# Revit family: RN 81037 Optipress-Aquaplus-Übergang
name_source: partatom
category: Rohrformteile
units: mm (PartAtom-declared; Revit-internal decimal feet)

## family parameters
Arbeitsebenenbasiert = Nein
Beim Laden mit Abzugskörper schneiden = Nein
Bemaßung runder Anschluss = Durchmesser verwenden
Gemeinsam genutzt = Nein
Immer vertikal = Ja
Teiletyp = Verbindung

## types (9) — shared parameters
1.010.00.2 Blattnummer der Richtlinie = 29
1.010.00.3 Ausgabedatum (Monat) der Richtlinie = 201308
1.010.00.4 Herstellername = R. Nussbaum AG
1.010.00.5 Revisionsdatum der Datei = 20190521
1.010.00.6 Webadresse des Herstellers = http://www.nussbaum.ch
1.100.00.4 Produktbezeichnung = Versorgung
1.110.00.2 Index = 4
1.110.00.4 Produktbezeichnung = Optipress
1.960/3L.00.8 Link (URL) = https://www.nussbaum.ch
29.700.00.4 Produktname = Optipress-Aquaplus-Übergang, für flachdichtende Verschraubungen
29.700.00.5 Produktkennung = 2
29.700.00.6 Querschnittsform = 1
29.700.00.7 Nennweitensystem = DN
29.700.00.8 Nenndrucksystem = PN
29.710.02.4 Nenndruck = 16
29.710.02.5 max. zul. Überdruck [hPa] = 1600
29.710.02.7 max. zul. Dauer-Betriebsdruck [hPa] = 1600
29.710.02.9 max. zul. Dauer-Betriebstemperatur [°C] = 95
Connector Visibility = Nein
EnclosingSpace Visibility = Nein

## per-type parameters (varying)
| type | 1.800.00.3 TGA-Nummer | 1.810.00.3 Hersteller-Bestellnummer | 1.810.00.4 DATANORM-Nummer | 1.810.00.5 StLB-Nummer | 1.810.00.6 GTIN-Nummer | 29.710.02.10 Formstück-Gewicht [kg] | 29.710.02.3 Benennung | CONNECTOR0_DIAMETER_dX_0r | CONNECTOR0_dX_01 | CONNECTOR0_ref_dX | CONNECTOR1_DIAMETER_dX_0r | CONNECTOR1_dX_00 | CONNECTOR1_dX_01 | CONNECTOR1_ref_dX | R. Nussbaum AG 81037.21 de Visibility | R. Nussbaum AG 81037.22 de Visibility | R. Nussbaum AG 81037.23 de Visibility | R. Nussbaum AG 81037.24 de Visibility | R. Nussbaum AG 81037.25 de Visibility | R. Nussbaum AG 81037.26 de Visibility | R. Nussbaum AG 81037.27 de Visibility | R. Nussbaum AG 81037.28 de Visibility | R. Nussbaum AG 81037.29 de Visibility |
| 81037.21, Optipress-Aquaplus-Übergang, für flachdichtende Verschraubungen, DN=12x15, L=43 | 01900400000000000000000000000000000000000000000039000000000000000001 | 81037.21 | 81037.21 | 266.553 | 7612945713803 | 0.041 | Optipress-Aquaplus-Übergang, für flachdichtende Verschraubungen, DN=12x15, L=43 | 12 mm  [stored 0.0393701 ft] | 22 mm | 22 mm | 15 mm  [stored 0.0492126 ft] | 30 mm  [stored 0.0984252 ft] | 43 mm  [stored 0.141076 ft] | 30 mm  [stored 0.0984252 ft] | Ja | Nein | Nein | Nein | Nein | Nein | Nein | Nein | Nein |
| 81037.22, Optipress-Aquaplus-Übergang, für flachdichtende Verschraubungen, DN=15x20, L=49 | 01900400000000000000000000000000000000000000000039000000000000000002 | 81037.22 | 81037.22 | 266.553 | 7612945654274 | 0.059 | Optipress-Aquaplus-Übergang, für flachdichtende Verschraubungen, DN=15x20, L=49 | 15 mm  [stored 0.0492126 ft] | 22 mm | 22 mm | 20 mm | 28 mm | 43 mm  [stored 0.141076 ft] | 28 mm | Nein | Ja | Nein | Nein | Nein | Nein | Nein | Nein | Nein |
| 81037.23, Optipress-Aquaplus-Übergang, für flachdichtende Verschraubungen, DN=15x20, L=49 | 01900400000000000000000000000000000000000000000039000000000000000003 | 81037.23 | 81037.23 | 266.553 | 7612945654281 | 0.076 | Optipress-Aquaplus-Übergang, für flachdichtende Verschraubungen, DN=15x20, L=49 | 15 mm  [stored 0.0492126 ft] | 22 mm | 22 mm | 20 mm | 28 mm | 43 mm  [stored 0.141076 ft] | 28 mm | Nein | Nein | Ja | Nein | Nein | Nein | Nein | Nein | Nein |
| 81037.24, Optipress-Aquaplus-Übergang, für flachdichtende Verschraubungen, DN=20x25, L=50 | 01900400000000000000000000000000000000000000000039000000000000000004 | 81037.24 | 81037.24 | 266.554 | 7612945654298 | 0.115 | Optipress-Aquaplus-Übergang, für flachdichtende Verschraubungen, DN=20x25, L=50 | 20 mm | 24 mm | 24 mm | 25 mm  [stored 0.082021 ft] | 33 mm  [stored 0.108268 ft] | 50 mm  [stored 0.164042 ft] | 33 mm  [stored 0.108268 ft] | Nein | Nein | Nein | Ja | Nein | Nein | Nein | Nein | Nein |
| 81037.25, Optipress-Aquaplus-Übergang, für flachdichtende Verschraubungen, DN=25x32, L=53 | 01900400000000000000000000000000000000000000000039000000000000000005 | 81037.25 | 81037.25 | 266.555 | 7612945654502 | 0.162 | Optipress-Aquaplus-Übergang, für flachdichtende Verschraubungen, DN=25x32, L=53 | 25 mm  [stored 0.082021 ft] | 24 mm | 24 mm | 32 mm | 34 mm | 53 mm | 34 mm | Nein | Nein | Nein | Nein | Ja | Nein | Nein | Nein | Nein |
| 81037.26, Optipress-Aquaplus-Übergang, für flachdichtende Verschraubungen, DN=32x40, L=56 | 01900400000000000000000000000000000000000000000039000000000000000006 | 81037.26 | 81037.26 | 266.556 | 7612945654519 | 0.209 | Optipress-Aquaplus-Übergang, für flachdichtende Verschraubungen, DN=32x40, L=56 | 32 mm | 26 mm | 26 mm | 40 mm | 37 mm | 56 mm | 37 mm | Nein | Nein | Nein | Nein | Nein | Ja | Nein | Nein | Nein |
| 81037.27, Optipress-Aquaplus-Übergang, für flachdichtende Verschraubungen, DN=40, L=63 | 01900400000000000000000000000000000000000000000039000000000000000007 | 81037.27 | 81037.27 | 266.557 | 7612945654526 | 0.309 | Optipress-Aquaplus-Übergang, für flachdichtende Verschraubungen, DN=40, L=63 | 40 mm | 36 mm | 36 mm | 40 mm | 44 mm | 63 mm | 44 mm | Nein | Nein | Nein | Nein | Nein | Nein | Ja | Nein | Nein |
| 81037.28, Optipress-Aquaplus-Übergang, für flachdichtende Verschraubungen, DN=50, L=76 | 01900400000000000000000000000000000000000000000039000000000000000008 | 81037.28 | 81037.28 | 266.558 | 7612945654533 | 0.459 | Optipress-Aquaplus-Übergang, für flachdichtende Verschraubungen, DN=50, L=76 | 50 mm  [stored 0.164042 ft] | 40 mm | 40 mm | 65 mm | 49 mm | 76 mm | 49 mm | Nein | Nein | Nein | Nein | Nein | Nein | Nein | Ja | Nein |
| 81037.29, Optipress-Aquaplus-Übergang, für flachdichtende Verschraubungen, DN=25, L=55 | 01900400000000000000000000000000000000000000000039000000000000000009 | 81037.29 | 81037.29 | 266.555 | 7612945693303 | 0.171 | Optipress-Aquaplus-Übergang, für flachdichtende Verschraubungen, DN=25, L=55 | 25 mm  [stored 0.082021 ft] | 24 mm | 24 mm | 25 mm  [stored 0.082021 ft] | 38 mm | 55 mm | 38 mm | Nein | Nein | Nein | Nein | Nein | Nein | Nein | Nein | Ja |

note: column(s) folded — value = type name in every type: 1.800.00.4 Kommentarfeld

note: [stored X ft] marks values corroborated as IEEE doubles in the binary element streams (Revit-internal decimal feet)

## geometry (parser evidence)
native form markers: Sweep x3
no freeform markers — native parametric forms only
